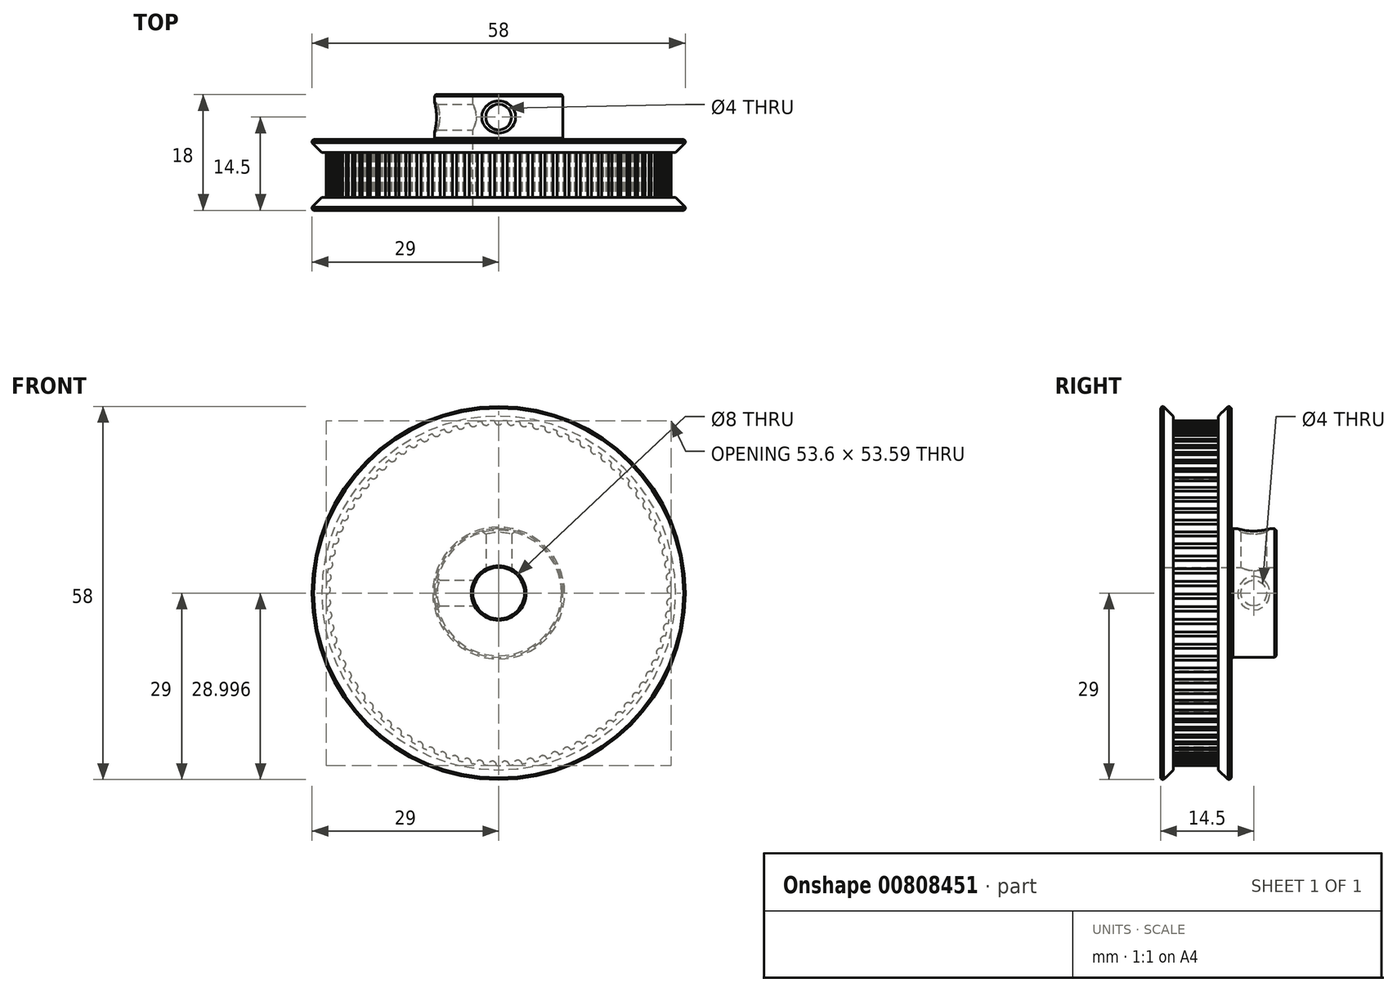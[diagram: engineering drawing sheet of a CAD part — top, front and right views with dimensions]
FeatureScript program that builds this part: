
annotation { "Feature Type Name" : "Feature", "Feature Type Description" : "" }
export const myFeature = defineFeature(function(context is Context, id is Id, definition is map)
    precondition{}
    {
        {
            var Q0;
            Q0=qCreatedBy(makeId("Front.planeOp"),FACE);
            var sketch = newSketch(context, id + "F0", { "sketchPlane" : qUnion([Q0])});
            skCircle(sketch, "E0", {"center": v(0, 0) * mm, "radius": 26.8 * mm});
            skSolve(sketch);
        }
        {
            var Q0;
            Q0=qSketchRegion(id+"F0",true);
            extrude(context, id + "F1", {"entities" : qUnion([Q0]), "depth" : 7 * mm, "offsetDistance" : 25 * mm, "symmetric" : true});
        }
        {
            var Q0;
            Q0=makeQuery(id+"F1.opExtrude","CAP_FACE",FACE,{"disambiguationData":[OSD([sQuery(id+"F0.wireOp",EDGE,"E0")])],"isStart":false});
            var sketch = newSketch(context, id + "F2", { "sketchPlane" : qUnion([Q0])});
            skCircle(sketch, "E1", {"center": v(0, 0) * mm, "radius": 29 * mm});
            skSolve(sketch);
        }
        {
            var Q0;
            Q0=qSketchRegion(id+"F2",true);
            extrude(context, id + "F3", {"entities" : qUnion([Q0]), "operationType" : NewBodyOperationType.ADD, "depth" : 2 * mm, "offsetDistance" : 25 * mm});
        }
        {
            var Q0;
            Q0=makeQuery(id+"F1.opExtrude","CAP_FACE",FACE,{"disambiguationData":[OSD([sQuery(id+"F0.wireOp",EDGE,"E0")])],"isStart":true});
            var sketch = newSketch(context, id + "F4", { "sketchPlane" : qUnion([Q0])});
            skCircle(sketch, "E2", {"center": v(0, 0) * mm, "radius": 29 * mm});
            skSolve(sketch);
        }
        {
            var Q0;
            Q0=qSketchRegion(id+"F4",true);
            extrude(context, id + "F5", {"entities" : qUnion([Q0]), "operationType" : NewBodyOperationType.ADD, "depth" : 2 * mm, "offsetDistance" : 25 * mm});
        }
        {
            var Q0;
            Q0=makeQuery(id+"F5.opExtrude","CAP_FACE",FACE,{"disambiguationData":[OSD([sQuery(id+"F4.wireOp",EDGE,"E2")])],"isStart":false});
            var sketch = newSketch(context, id + "F6", { "sketchPlane" : qUnion([Q0])});
            skCircle(sketch, "E3", {"center": v(0, 0) * mm, "radius": 10 * mm});
            skSolve(sketch);
        }
        {
            var Q0;
            Q0=qSketchRegion(id+"F6",true);
            extrude(context, id + "F7", {"entities" : qUnion([Q0]), "operationType" : NewBodyOperationType.ADD, "depth" : 7 * mm, "offsetDistance" : 25 * mm});
        }
        {
            var Q0;
            Q0=makeQuery(id+"F7.opExtrude","CAP_FACE",FACE,{"disambiguationData":[OSD([sQuery(id+"F6.wireOp",EDGE,"E3")])],"isStart":false});
            var sketch = newSketch(context, id + "F8", { "sketchPlane" : qUnion([Q0])});
            skCircle(sketch, "E4", {"center": v(0, 0) * mm, "radius": 4 * mm});
            skSolve(sketch);
        }
        {
            var Q0;
            Q0=qSketchRegion(id+"F8",true);
            extrude(context, id + "F9", {"entities" : qUnion([Q0]), "operationType" : NewBodyOperationType.REMOVE, "endBound" : BoundingType.THROUGH_ALL, "oppositeDirection" : true, "depth" : 25 * mm, "offsetDistance" : 25 * mm});
        }
        {
            var Q0;
            Q0=makeQuery(id+"F3.opExtrude","CAP_FACE",FACE,{"disambiguationData":[OSD([sQuery(id+"F2.wireOp",EDGE,"E1")])],"isStart":true});
            var sketch = newSketch(context, id + "F10", { "sketchPlane" : qUnion([Q0])});
            skCircle(sketch, "E5", {"center": v(0, 0) * mm, "radius": 26.8 * mm, "construction": true});
            skLineSegment(sketch, "E6", {"start": v(0, 0) * mm, "end": v(0, 26.8) * mm, "construction": true});
            skCircle(sketch, "E7", {"center": v(0, 26.8) * mm, "radius": 0.65 * mm});
            skCircle(sketch, "E8.1.0", {"center": v(-1.98, 26.73) * mm, "radius": 0.65 * mm});
            skCircle(sketch, "E8.2.0", {"center": v(-3.95, 26.5) * mm, "radius": 0.65 * mm});
            skCircle(sketch, "E8.3.0", {"center": v(-5.9, 26.14) * mm, "radius": 0.65 * mm});
            skCircle(sketch, "E8.4.0", {"center": v(-7.8, 25.64) * mm, "radius": 0.65 * mm});
            skCircle(sketch, "E8.5.0", {"center": v(-9.68, 25) * mm, "radius": 0.65 * mm});
            skCircle(sketch, "E8.6.0", {"center": v(-11.5, 24.2) * mm, "radius": 0.65 * mm});
            skCircle(sketch, "E8.7.0", {"center": v(-13.26, 23.3) * mm, "radius": 0.65 * mm});
            skCircle(sketch, "E8.8.0", {"center": v(-14.94, 22.25) * mm, "radius": 0.65 * mm});
            skCircle(sketch, "E8.9.0", {"center": v(-16.54, 21.08) * mm, "radius": 0.65 * mm});
            skCircle(sketch, "E8.10.0", {"center": v(-18.06, 19.8) * mm, "radius": 0.65 * mm});
            skCircle(sketch, "E8.11.0", {"center": v(-19.47, 18.42) * mm, "radius": 0.65 * mm});
            skCircle(sketch, "E8.12.0", {"center": v(-20.78, 16.93) * mm, "radius": 0.65 * mm});
            skCircle(sketch, "E8.13.0", {"center": v(-21.97, 15.35) * mm, "radius": 0.65 * mm});
            skCircle(sketch, "E8.14.0", {"center": v(-23.04, 13.68) * mm, "radius": 0.65 * mm});
            skCircle(sketch, "E8.15.0", {"center": v(-24, 11.95) * mm, "radius": 0.65 * mm});
            skCircle(sketch, "E8.16.0", {"center": v(-24.8, 10.14) * mm, "radius": 0.65 * mm});
            skCircle(sketch, "E8.17.0", {"center": v(-25.49, 8.28) * mm, "radius": 0.65 * mm});
            skCircle(sketch, "E8.18.0", {"center": v(-26.03, 6.38) * mm, "radius": 0.65 * mm});
            skCircle(sketch, "E8.19.0", {"center": v(-26.43, 4.44) * mm, "radius": 0.65 * mm});
            skCircle(sketch, "E8.20.0", {"center": v(-26.69, 2.47) * mm, "radius": 0.65 * mm});
            skCircle(sketch, "E8.21.0", {"center": v(-26.8, 0.5) * mm, "radius": 0.65 * mm});
            skCircle(sketch, "E8.22.0", {"center": v(-26.76, -1.49) * mm, "radius": 0.65 * mm});
            skCircle(sketch, "E8.23.0", {"center": v(-26.58, -3.46) * mm, "radius": 0.65 * mm});
            skCircle(sketch, "E8.24.0", {"center": v(-26.25, -5.41) * mm, "radius": 0.65 * mm});
            skCircle(sketch, "E8.25.0", {"center": v(-25.78, -7.33) * mm, "radius": 0.65 * mm});
            skCircle(sketch, "E8.26.0", {"center": v(-25.16, -9.22) * mm, "radius": 0.65 * mm});
            skCircle(sketch, "E8.27.0", {"center": v(-24.42, -11.05) * mm, "radius": 0.65 * mm});
            skCircle(sketch, "E8.28.0", {"center": v(-23.53, -12.82) * mm, "radius": 0.65 * mm});
            skCircle(sketch, "E8.29.0", {"center": v(-22.52, -14.53) * mm, "radius": 0.65 * mm});
            skCircle(sketch, "E8.30.0", {"center": v(-21.39, -16.15) * mm, "radius": 0.65 * mm});
            skCircle(sketch, "E8.31.0", {"center": v(-20.14, -17.69) * mm, "radius": 0.65 * mm});
            skCircle(sketch, "E8.32.0", {"center": v(-18.77, -19.12) * mm, "radius": 0.65 * mm});
            skCircle(sketch, "E8.33.0", {"center": v(-17.31, -20.46) * mm, "radius": 0.65 * mm});
            skCircle(sketch, "E8.34.0", {"center": v(-15.75, -21.68) * mm, "radius": 0.65 * mm});
            skCircle(sketch, "E8.35.0", {"center": v(-14.1, -22.79) * mm, "radius": 0.65 * mm});
            skCircle(sketch, "E8.36.0", {"center": v(-12.39, -23.77) * mm, "radius": 0.65 * mm});
            skCircle(sketch, "E8.37.0", {"center": v(-10.6, -24.62) * mm, "radius": 0.65 * mm});
            skCircle(sketch, "E8.38.0", {"center": v(-8.75, -25.33) * mm, "radius": 0.65 * mm});
            skCircle(sketch, "E8.39.0", {"center": v(-6.86, -25.9) * mm, "radius": 0.65 * mm});
            skCircle(sketch, "E8.40.0", {"center": v(-4.92, -26.34) * mm, "radius": 0.65 * mm});
            skCircle(sketch, "E8.41.0", {"center": v(-2.97, -26.64) * mm, "radius": 0.65 * mm});
            skCircle(sketch, "E8.42.0", {"center": v(-1, -26.78) * mm, "radius": 0.65 * mm});
            skCircle(sketch, "E8.43.0", {"center": v(1, -26.78) * mm, "radius": 0.65 * mm});
            skCircle(sketch, "E8.44.0", {"center": v(2.97, -26.64) * mm, "radius": 0.65 * mm});
            skCircle(sketch, "E8.45.0", {"center": v(4.92, -26.34) * mm, "radius": 0.65 * mm});
            skCircle(sketch, "E8.46.0", {"center": v(6.86, -25.9) * mm, "radius": 0.65 * mm});
            skCircle(sketch, "E8.47.0", {"center": v(8.75, -25.33) * mm, "radius": 0.65 * mm});
            skCircle(sketch, "E8.48.0", {"center": v(10.6, -24.62) * mm, "radius": 0.65 * mm});
            skCircle(sketch, "E8.49.0", {"center": v(12.39, -23.77) * mm, "radius": 0.65 * mm});
            skCircle(sketch, "E8.50.0", {"center": v(14.1, -22.79) * mm, "radius": 0.65 * mm});
            skCircle(sketch, "E8.51.0", {"center": v(15.75, -21.68) * mm, "radius": 0.65 * mm});
            skCircle(sketch, "E8.52.0", {"center": v(17.31, -20.46) * mm, "radius": 0.65 * mm});
            skCircle(sketch, "E8.53.0", {"center": v(18.77, -19.12) * mm, "radius": 0.65 * mm});
            skCircle(sketch, "E8.54.0", {"center": v(20.14, -17.69) * mm, "radius": 0.65 * mm});
            skCircle(sketch, "E8.55.0", {"center": v(21.39, -16.15) * mm, "radius": 0.65 * mm});
            skCircle(sketch, "E8.56.0", {"center": v(22.52, -14.53) * mm, "radius": 0.65 * mm});
            skCircle(sketch, "E8.57.0", {"center": v(23.53, -12.82) * mm, "radius": 0.65 * mm});
            skCircle(sketch, "E8.58.0", {"center": v(24.42, -11.05) * mm, "radius": 0.65 * mm});
            skCircle(sketch, "E8.59.0", {"center": v(25.16, -9.22) * mm, "radius": 0.65 * mm});
            skCircle(sketch, "E8.60.0", {"center": v(25.78, -7.33) * mm, "radius": 0.65 * mm});
            skCircle(sketch, "E8.61.0", {"center": v(26.25, -5.41) * mm, "radius": 0.65 * mm});
            skCircle(sketch, "E8.62.0", {"center": v(26.58, -3.46) * mm, "radius": 0.65 * mm});
            skCircle(sketch, "E8.63.0", {"center": v(26.76, -1.49) * mm, "radius": 0.65 * mm});
            skCircle(sketch, "E8.64.0", {"center": v(26.8, 0.5) * mm, "radius": 0.65 * mm});
            skCircle(sketch, "E8.65.0", {"center": v(26.69, 2.47) * mm, "radius": 0.65 * mm});
            skCircle(sketch, "E8.66.0", {"center": v(26.43, 4.44) * mm, "radius": 0.65 * mm});
            skCircle(sketch, "E8.67.0", {"center": v(26.03, 6.38) * mm, "radius": 0.65 * mm});
            skCircle(sketch, "E8.68.0", {"center": v(25.49, 8.28) * mm, "radius": 0.65 * mm});
            skCircle(sketch, "E8.69.0", {"center": v(24.8, 10.14) * mm, "radius": 0.65 * mm});
            skCircle(sketch, "E8.70.0", {"center": v(24, 11.95) * mm, "radius": 0.65 * mm});
            skCircle(sketch, "E8.71.0", {"center": v(23.04, 13.68) * mm, "radius": 0.65 * mm});
            skCircle(sketch, "E8.72.0", {"center": v(21.97, 15.35) * mm, "radius": 0.65 * mm});
            skCircle(sketch, "E8.73.0", {"center": v(20.78, 16.93) * mm, "radius": 0.65 * mm});
            skCircle(sketch, "E8.74.0", {"center": v(19.47, 18.42) * mm, "radius": 0.65 * mm});
            skCircle(sketch, "E8.75.0", {"center": v(18.06, 19.8) * mm, "radius": 0.65 * mm});
            skCircle(sketch, "E8.76.0", {"center": v(16.54, 21.08) * mm, "radius": 0.65 * mm});
            skCircle(sketch, "E8.77.0", {"center": v(14.94, 22.25) * mm, "radius": 0.65 * mm});
            skCircle(sketch, "E8.78.0", {"center": v(13.26, 23.3) * mm, "radius": 0.65 * mm});
            skCircle(sketch, "E8.79.0", {"center": v(11.5, 24.2) * mm, "radius": 0.65 * mm});
            skCircle(sketch, "E8.80.0", {"center": v(9.68, 25) * mm, "radius": 0.65 * mm});
            skCircle(sketch, "E8.81.0", {"center": v(7.8, 25.64) * mm, "radius": 0.65 * mm});
            skCircle(sketch, "E8.82.0", {"center": v(5.9, 26.14) * mm, "radius": 0.65 * mm});
            skCircle(sketch, "E8.83.0", {"center": v(3.95, 26.5) * mm, "radius": 0.65 * mm});
            skCircle(sketch, "E8.84.0", {"center": v(1.98, 26.73) * mm, "radius": 0.65 * mm});
            skSolve(sketch);
        }
        {
            var Q0;
            Q0=qSketchRegion(id+"F10",true);
            extrude(context, id + "F11", {"entities" : qUnion([Q0]), "operationType" : NewBodyOperationType.REMOVE, "depth" : 7 * mm, "offsetDistance" : 25 * mm});
        }
        {
            var Q0;
            Q0=makeQuery(id+"F3.opExtrude","CAP_EDGE",EDGE,{"disambiguationData":[OSD([sQuery(id+"F2.wireOp",EDGE,"E1")])],"isStart":true});
            var Q1;
            Q1=makeQuery(id+"F5.opExtrude","CAP_EDGE",EDGE,{"disambiguationData":[OSD([sQuery(id+"F4.wireOp",EDGE,"E2")])],"isStart":true});
            chamfer(context, id + "F12", {"entities" : qUnion([Q0, Q1]), "width" : 1.5 * mm, "tangentPropagation" : true});
        }
        {
            var Q0;
            Q0=qCreatedBy(makeId("Top.planeOp"),FACE);
            var sketch = newSketch(context, id + "F13", { "sketchPlane" : qUnion([Q0])});
            skLineSegment(sketch, "E9", {"start": v(0, 0) * mm, "end": v(0, 12.5) * mm, "construction": true});
            skCircle(sketch, "E10", {"center": v(0, 9) * mm, "radius": 2 * mm});
            skSolve(sketch);
        }
        {
            var Q0;
            Q0=qSketchRegion(id+"F13",true);
            extrude(context, id + "F14", {"entities" : qUnion([Q0]), "operationType" : NewBodyOperationType.REMOVE, "endBound" : BoundingType.THROUGH_ALL, "depth" : 25 * mm, "offsetDistance" : 25 * mm});
        }
        {
            var Q0;
            Q0=qCreatedBy(makeId("Right.planeOp"),FACE);
            var sketch = newSketch(context, id + "F15", { "sketchPlane" : qUnion([Q0])});
            skLineSegment(sketch, "E11", {"start": v(0, 0) * mm, "end": v(12.5, 0) * mm, "construction": true});
            skCircle(sketch, "E12", {"center": v(9, 0) * mm, "radius": 2 * mm});
            skSolve(sketch);
        }
        {
            var Q0;
            Q0=qSketchRegion(id+"F15",true);
            extrude(context, id + "F16", {"entities" : qUnion([Q0]), "operationType" : NewBodyOperationType.REMOVE, "endBound" : BoundingType.THROUGH_ALL, "oppositeDirection" : true, "depth" : 25 * mm, "offsetDistance" : 25 * mm});
        }
        {
            var Q0;
            Q0=makeQuery(id+"F14.boolean.opBoolean","INTERSECT",EDGE,{"derivedFrom":[makeQuery(id+"F7.opExtrude","SWEPT_FACE",FACE,{"disambiguationData":[OSD([sQuery(id+"F6.wireOp",EDGE,"E3")])]}),makeQuery(id+"F14.opExtrude","SWEPT_FACE",FACE,{"disambiguationData":[OSD([sQuery(id+"F13.wireOp",EDGE,"E10")])]})]});
            var Q1;
            Q1=makeQuery(id+"F16.boolean.opBoolean","INTERSECT",EDGE,{"derivedFrom":[makeQuery(id+"F7.opExtrude","SWEPT_FACE",FACE,{"disambiguationData":[OSD([sQuery(id+"F6.wireOp",EDGE,"E3")])]}),makeQuery(id+"F16.opExtrude","SWEPT_FACE",FACE,{"disambiguationData":[OSD([sQuery(id+"F15.wireOp",EDGE,"E12")])]})]});
            chamfer(context, id + "F17", {"entities" : qUnion([Q0, Q1]), "width" : 0.5 * mm, "tangentPropagation" : true});
        }
        {
            var Q0;
            Q0=makeQuery(id+"F7.opExtrude","CAP_FACE",FACE,{"disambiguationData":[OSD([sQuery(id+"F6.wireOp",EDGE,"E3")])],"isStart":false});
            var Q1;
            Q1=makeQuery(id+"F7.opExtrude","CAP_EDGE",EDGE,{"disambiguationData":[OSD([sQuery(id+"F6.wireOp",EDGE,"E3")])],"isStart":true});
            var Q2;
            Q2=makeQuery(id+"F5.opExtrude","CAP_FACE",FACE,{"disambiguationData":[OSD([sQuery(id+"F4.wireOp",EDGE,"E2")])],"isStart":false});
            var Q3;
            Q3=makeQuery(id+"F3.opExtrude","CAP_FACE",FACE,{"disambiguationData":[OSD([sQuery(id+"F2.wireOp",EDGE,"E1")])],"isStart":false});
            chamfer(context, id + "F18", {"entities" : qUnion([Q0, Q1, Q2, Q3]), "width" : 0.25 * mm, "tangentPropagation" : true});
        }
    });
